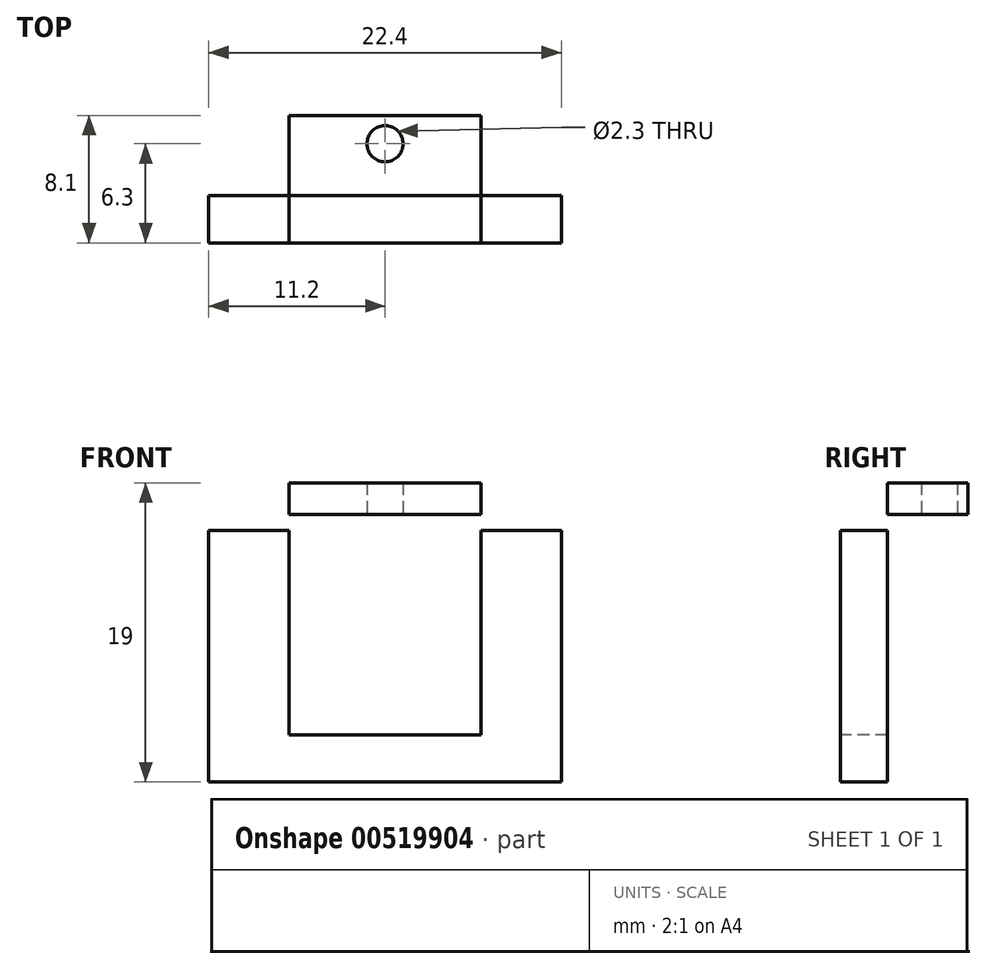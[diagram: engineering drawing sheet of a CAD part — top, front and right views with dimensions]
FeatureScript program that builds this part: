
annotation { "Feature Type Name" : "Feature", "Feature Type Description" : "" }
export const myFeature = defineFeature(function(context is Context, id is Id, definition is map)
    precondition{}
    {
        {
            var Q0;
            Q0=qCreatedBy(makeId("Top.planeOp"),FACE);
            var sketch = newSketch(context, id + "F0", { "sketchPlane" : qUnion([Q0])});
            skLineSegment(sketch, "E0", {"start": v(11.2, 0) * mm, "end": v(22.4, 0) * mm});
            skLineSegment(sketch, "E1", {"start": v(17.3, 5.1) * mm, "end": v(11.2, 5.1) * mm});
            skLineSegment(sketch, "E2", {"start": v(11.2, 5.1) * mm, "end": v(11.2, 3.3) * mm, "construction": true});
            skCircle(sketch, "E3", {"center": v(11.2, 3.3) * mm, "radius": 1.15 * mm});
            skPoint(sketch, "E4.endSnap0", {"position": v(11.2, 4.2) * mm});
            skLineSegment(sketch, "E5", {"start": v(22.4, -3) * mm, "end": v(22.4, 0) * mm});
            skLineSegment(sketch, "E6", {"start": v(11.2, 0) * mm, "end": v(17.3, 0) * mm});
            skLineSegment(sketch, "E7", {"start": v(17.3, 0) * mm, "end": v(17.3, 5.1) * mm});
            skLineSegment(sketch, "E8.MirrorCS", {"start": v(5.1, 5.1) * mm, "end": v(11.2, 5.1) * mm});
            skLineSegment(sketch, "E9.MirrorCS", {"start": v(5.1, 0) * mm, "end": v(5.1, 5.1) * mm});
            skLineSegment(sketch, "E10.MirrorCS", {"start": v(11.2, 0) * mm, "end": v(5.1, 0) * mm});
            skLineSegment(sketch, "E11.MirrorCS", {"start": v(11.2, 0) * mm, "end": v(0, 0) * mm});
            skLineSegment(sketch, "E12.MirrorCS", {"start": v(0, -3) * mm, "end": v(0, 0) * mm});
            skLineSegment(sketch, "E13", {"start": v(0, -3) * mm, "end": v(22.4, -3) * mm});
            skLineSegment(sketch, "E14", {"start": v(5.1, 0) * mm, "end": v(5.1, -3) * mm});
            skLineSegment(sketch, "E15", {"start": v(17.3, 0) * mm, "end": v(17.3, -3) * mm});
            skSolve(sketch);
        }
        {
            var Q0;
            Q0=makeQuery(id+"F0.imprint","IMPRINT",FACE,{"disambiguationData":[TD([[makeQuery(id+"F0.imprint","IMPRINT",EDGE,{"derivedFrom":sQuery(id+"F0.wireOp",EDGE,"E1")}),1.0]])]});
            var Q1;
            {var subQ4=sQuery(id+"F0.wireOp",EDGE,"E6");Q1=makeQuery(id+"F0.imprint","IMPRINT",FACE,{"disambiguationData":[TD([[makeQuery(id+"F0.imprint","IMPRINT",EDGE,{"derivedFrom":subQ4}),-1.0]])]});}
            extrude(context, id + "F1", {"entities" : qUnion([Q0, Q1]), "depth" : 2 * mm, "offsetDistance" : 25 * mm});
        }
        {
            var Q0;
            {var subQ2=sQuery(id+"F0.wireOp",EDGE,"E12.MirrorCS");Q0=makeQuery(id+"F0.imprint","IMPRINT",FACE,{"disambiguationData":[TD([[makeQuery(id+"F0.imprint","IMPRINT",EDGE,{"derivedFrom":subQ2}),-1.0]])]});}
            var Q1;
            {var subQ4=sQuery(id+"F0.wireOp",EDGE,"E6");Q1=makeQuery(id+"F0.imprint","IMPRINT",FACE,{"disambiguationData":[TD([[makeQuery(id+"F0.imprint","IMPRINT",EDGE,{"derivedFrom":subQ4}),-1.0]])]});}
            var Q2;
            Q2=makeQuery(id+"F0.imprint","IMPRINT",FACE,{"disambiguationData":[TD([[makeQuery(id+"F0.imprint","IMPRINT",EDGE,{"derivedFrom":sQuery(id+"F0.wireOp",EDGE,"E0")}),-1.0]])]});
            extrude(context, id + "F2", {"entities" : qUnion([Q0, Q1, Q2]), "operationType" : NewBodyOperationType.ADD, "oppositeDirection" : true, "depth" : 17 * mm, "offsetDistance" : 25 * mm});
        }
        {
            var Q0;
            Q0=makeQuery(id+"F2.opExtrude","CAP_FACE",FACE,{"disambiguationData":[OSD([sQuery(id+"F0.wireOp",EDGE,"E0"),sQuery(id+"F0.wireOp",EDGE,"E5"),sQuery(id+"F0.wireOp",EDGE,"E6"),sQuery(id+"F0.wireOp",EDGE,"E11.MirrorCS"),sQuery(id+"F0.wireOp",EDGE,"E12.MirrorCS"),sQuery(id+"F0.wireOp",EDGE,"E13")])],"isStart":false});
            var sketch = newSketch(context, id + "F3", { "sketchPlane" : qUnion([Q0])});
            skLineSegment(sketch, "E16.0.0", {"start": v(22.4, 3) * mm, "end": v(0, 3) * mm});
            skLineSegment(sketch, "E16.0.1", {"start": v(0, 3) * mm, "end": v(0, 0) * mm});
            skLineSegment(sketch, "E16.0.2", {"start": v(0, 0) * mm, "end": v(22.4, 0) * mm});
            skLineSegment(sketch, "E16.0.3", {"start": v(22.4, 0) * mm, "end": v(22.4, 3) * mm});
            skLineSegment(sketch, "E17", {"start": v(0, 3) * mm, "end": v(0, 40) * mm});
            skLineSegment(sketch, "E18", {"start": v(0, 40) * mm, "end": v(22.4, 40) * mm});
            skLineSegment(sketch, "E19", {"start": v(22.4, 40) * mm, "end": v(22.4, 3) * mm});
            skLineSegment(sketch, "E20", {"start": v(11.2, 40) * mm, "end": v(11.2, 30.8) * mm, "construction": true});
            skLineSegment(sketch, "E21", {"start": v(11.2, 30.8) * mm, "end": v(11.2, 35.8) * mm});
            skLineSegment(sketch, "E22", {"start": v(11.2, 35.8) * mm, "end": v(12.5, 35.8) * mm, "construction": true});
            skCircle(sketch, "E23", {"center": v(12.5, 35.8) * mm, "radius": 0.75 * mm});
            skLineSegment(sketch, "E24", {"start": v(11.2, 30.8) * mm, "end": v(18.45, 30.8) * mm, "construction": true});
            skCircle(sketch, "E25.MirrorC", {"center": v(12.5, 25.8) * mm, "radius": 0.75 * mm});
            skCircle(sketch, "E26.MirrorC", {"center": v(9.9, 25.8) * mm, "radius": 0.75 * mm});
            skCircle(sketch, "E27.MirrorC", {"center": v(9.9, 35.8) * mm, "radius": 0.75 * mm});
            skLineSegment(sketch, "E28", {"start": v(11.2, 30.8) * mm, "end": v(4.7, 30.8) * mm, "construction": true});
            skLineSegment(sketch, "E29", {"start": v(4.7, 30.8) * mm, "end": v(4.7, 32.4) * mm, "construction": true});
            skCircle(sketch, "E30", {"center": v(4.7, 32.4) * mm, "radius": 0.75 * mm});
            skCircle(sketch, "E31.MirrorC", {"center": v(4.7, 29.2) * mm, "radius": 0.75 * mm});
            skCircle(sketch, "E32.MirrorC", {"center": v(17.7, 29.2) * mm, "radius": 0.75 * mm});
            skCircle(sketch, "E33.MirrorC", {"center": v(17.7, 32.4) * mm, "radius": 0.75 * mm});
            skCircle(sketch, "E34", {"center": v(11.2, 30.8) * mm, "radius": 3.5 * mm});
            skPoint(sketch, "E35.visualSharp", {"position": v(0, 40) * mm});
            skLineSegment(sketch, "E35.filletArc", {"start": v(0, 40) * mm, "end": v(0, 40) * mm});
            skPoint(sketch, "E36.visualSharp", {"position": v(22.4, 40) * mm});
            skLineSegment(sketch, "E36.filletArc", {"start": v(22.4, 40) * mm, "end": v(22.4, 40) * mm});
            skSolve(sketch);
        }
        {
            var Q0;
            Q0=makeQuery(id+"F3.imprint","IMPRINT",FACE,{"disambiguationData":[TD([[makeQuery(id+"F3.imprint","IMPRINT",EDGE,{"derivedFrom":sQuery(id+"F3.wireOp",EDGE,"E16.0.0")}),1.0]])]});
            var Q1;
            Q1=makeQuery(id+"F3.imprint","IMPRINT",FACE,{"disambiguationData":[TD([[makeQuery(id+"F3.imprint","IMPRINT",EDGE,{"derivedFrom":sQuery(id+"F3.wireOp",EDGE,"E16.0.0")}),-1.0]])]});
            extrude(context, id + "F4", {"entities" : qUnion([Q0, Q1]), "operationType" : NewBodyOperationType.ADD, "oppositeDirection" : true, "depth" : 3 * mm, "offsetDistance" : 25 * mm});
        }
        {
            var Q0;
            {var subQ2=sQuery(id+"F0.wireOp",EDGE,"E12.MirrorCS");Q0=makeQuery(id+"F0.imprint","IMPRINT",FACE,{"disambiguationData":[TD([[makeQuery(id+"F0.imprint","IMPRINT",EDGE,{"derivedFrom":subQ2}),-1.0]])]});}
            var sketch = newSketch(context, id + "F5", { "sketchPlane" : qUnion([Q0])});
            skLineSegment(sketch, "E37.0.0", {"start": v(5.1, -3) * mm, "end": v(5.1, 0) * mm});
            skLineSegment(sketch, "E37.0.1", {"start": v(5.1, 0) * mm, "end": v(0, 0) * mm});
            skLineSegment(sketch, "E37.0.2", {"start": v(0, 0) * mm, "end": v(0, -3) * mm});
            skLineSegment(sketch, "E37.0.3", {"start": v(0, -3) * mm, "end": v(5.1, -3) * mm});
            skLineSegment(sketch, "E38.0.0", {"start": v(22.4, 0) * mm, "end": v(17.3, 0) * mm});
            skLineSegment(sketch, "E38.0.1", {"start": v(17.3, 0) * mm, "end": v(17.3, -3) * mm});
            skLineSegment(sketch, "E38.0.2", {"start": v(17.3, -3) * mm, "end": v(22.4, -3) * mm});
            skLineSegment(sketch, "E38.0.3", {"start": v(22.4, -3) * mm, "end": v(22.4, 0) * mm});
            skSolve(sketch);
        }
        {
            var Q0;
            Q0=qSketchRegion(id+"F5",true);
            extrude(context, id + "F6", {"entities" : qUnion([Q0]), "operationType" : NewBodyOperationType.REMOVE, "oppositeDirection" : true, "depth" : 1 * mm, "offsetDistance" : 25 * mm});
        }
    });
